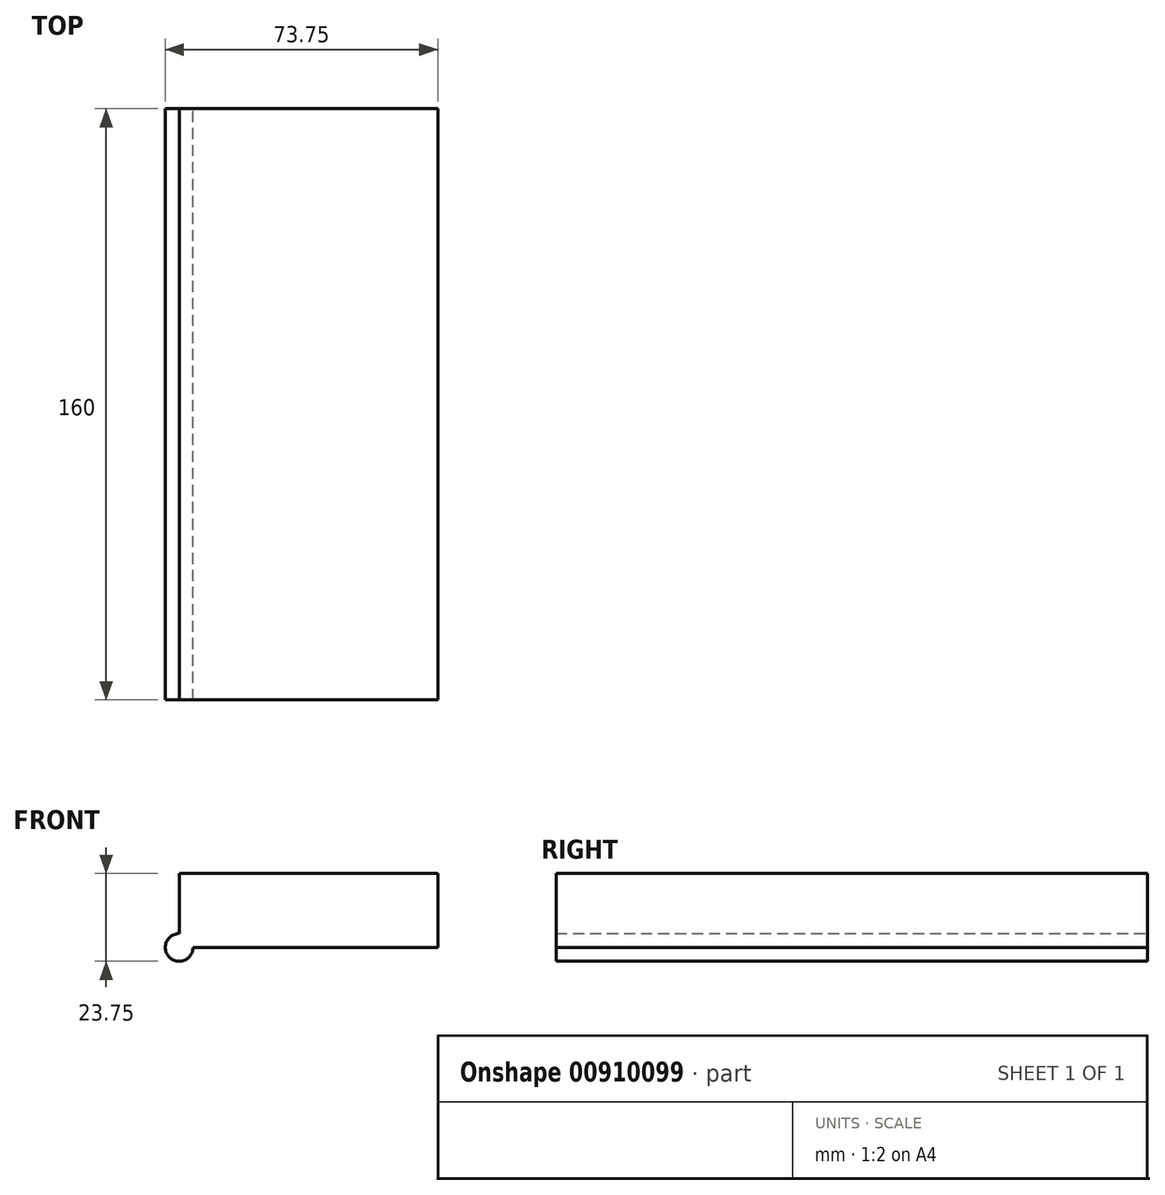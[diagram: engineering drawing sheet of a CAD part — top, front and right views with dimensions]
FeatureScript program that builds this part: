
annotation { "Feature Type Name" : "Feature", "Feature Type Description" : "" }
export const myFeature = defineFeature(function(context is Context, id is Id, definition is map)
    precondition{}
    {
        {
            var Q0;
            Q0=qCreatedBy(makeId("Front.planeOp"),FACE);
            var sketch = newSketch(context, id + "F0", { "sketchPlane" : qUnion([Q0])});
            skLineSegment(sketch, "E0.bottom", {"start": v(0, 0) * mm, "end": v(-70, 0) * mm});
            skLineSegment(sketch, "E0.top", {"start": v(0, 20) * mm, "end": v(-70, 20) * mm});
            skLineSegment(sketch, "E0.left", {"start": v(0, 0) * mm, "end": v(0, 20) * mm});
            skLineSegment(sketch, "E0.right", {"start": v(-70, 0) * mm, "end": v(-70, 20) * mm});
            skCircle(sketch, "E1", {"center": v(-70, 0) * mm, "radius": 3.75 * mm});
            skSolve(sketch);
        }
        {
            var Q0;
            Q0 = qSketchRegion(id + "F0", true);
            extrude(context, id + "F1", {"entities" : qUnion([Q0]), "endBound" : BoundingType.SYMMETRIC, "depth" : 160 * mm, "offsetDistance" : 25 * mm});
        }
    });
